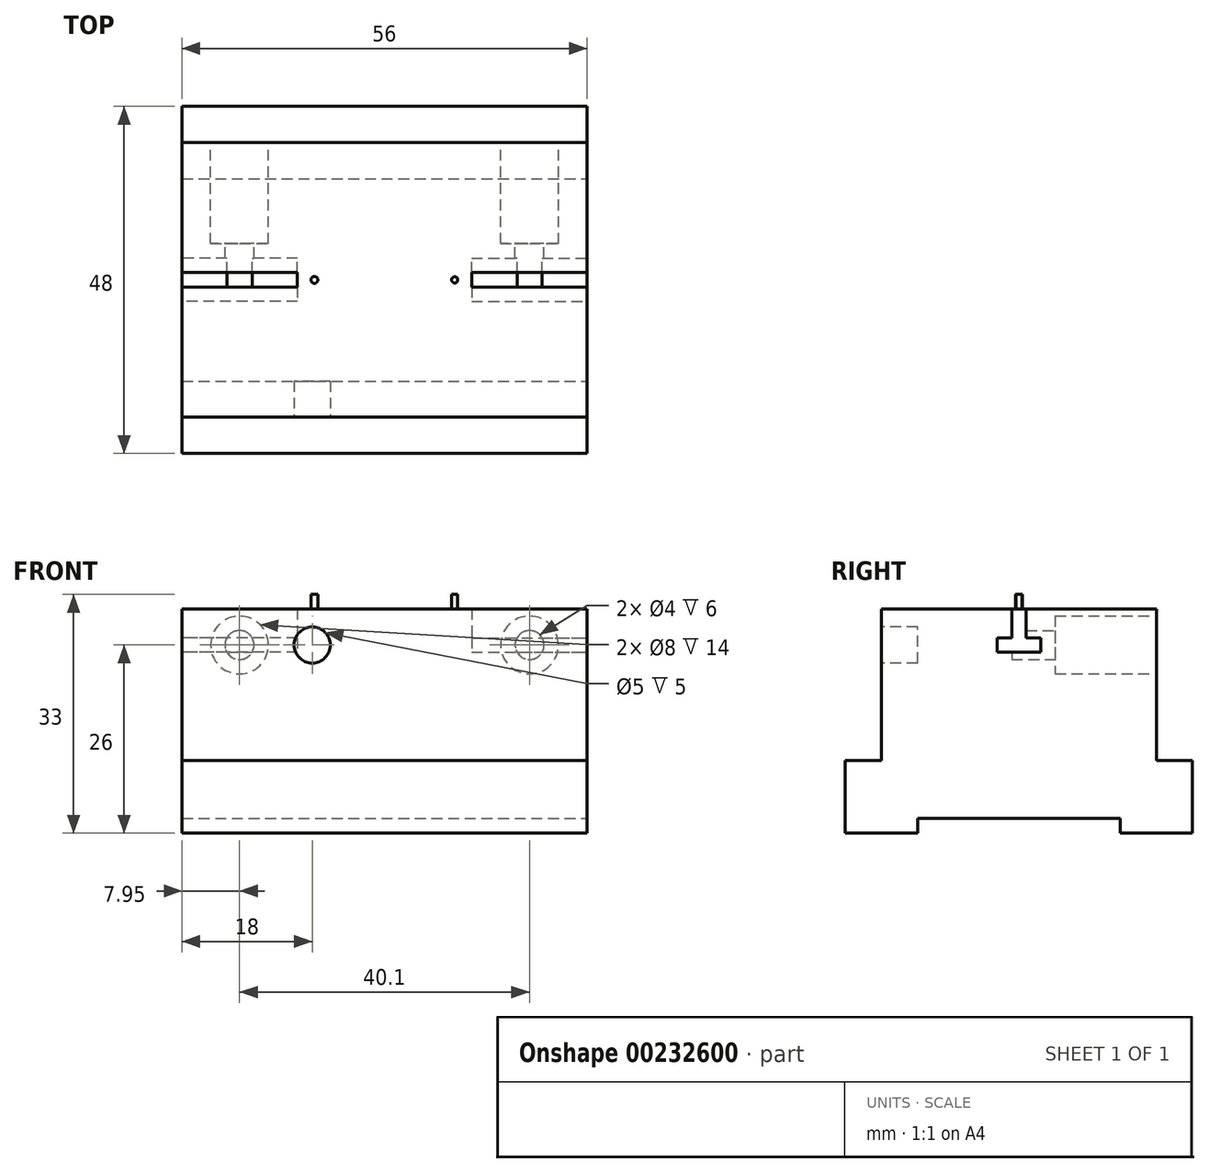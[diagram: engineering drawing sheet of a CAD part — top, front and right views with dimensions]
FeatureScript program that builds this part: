
annotation { "Feature Type Name" : "Feature", "Feature Type Description" : "" }
export const myFeature = defineFeature(function(context is Context, id is Id, definition is map)
    precondition{}
    {
        {
            var Q0;
            Q0=qCreatedBy(makeId("Top.planeOp"),FACE);
            var sketch = newSketch(context, id + "F0", { "sketchPlane" : qUnion([Q0])});
            skLineSegment(sketch, "E0.bottom", {"start": v(0, 0) * mm, "end": v(56, 0) * mm});
            skLineSegment(sketch, "E0.top", {"start": v(0, 48) * mm, "end": v(56, 48) * mm});
            skLineSegment(sketch, "E0.left", {"start": v(0, 0) * mm, "end": v(0, 48) * mm});
            skLineSegment(sketch, "E0.right", {"start": v(56, 0) * mm, "end": v(56, 48) * mm});
            skSolve(sketch);
        }
        {
            var Q0;
            Q0 = qSketchRegion(id + "F0", true);
            extrude(context, id + "F1", {"entities" : qUnion([Q0]), "oppositeDirection" : true, "depth" : 31 * mm});
        }
        {
            var Q0;
            Q0=qCreatedBy(makeId("Top.planeOp"),FACE);
            var sketch = newSketch(context, id + "F2", { "sketchPlane" : qUnion([Q0])});
            skCircle(sketch, "E1", {"center": v(18.3, 24) * mm, "radius": 0.47 * mm});
            skCircle(sketch, "E2", {"center": v(37.7, 24) * mm, "radius": 0.42 * mm});
            skSolve(sketch);
        }
        {
            var Q0;
            Q0 = qSketchRegion(id + "F2", true);
            extrude(context, id + "F3", {"entities" : qUnion([Q0]), "operationType" : NewBodyOperationType.ADD, "depth" : 2 * mm});
        }
        {
            var Q0;
            Q0=makeQuery(id+"F1.opExtrude","SWEPT_FACE",FACE,{"disambiguationData":[OSD([sQuery(id+"F0.wireOp",EDGE,"E0.right")])]});
            var sketch = newSketch(context, id + "F4", { "sketchPlane" : qUnion([Q0])});
            skLineSegment(sketch, "E3", {"start": v(23, 0) * mm, "end": v(23, -4) * mm});
            skLineSegment(sketch, "E4", {"start": v(23, -4) * mm, "end": v(21, -4) * mm});
            skLineSegment(sketch, "E5", {"start": v(21, -4) * mm, "end": v(21, -6) * mm});
            skLineSegment(sketch, "E6", {"start": v(21, -6) * mm, "end": v(27, -6) * mm});
            skLineSegment(sketch, "E7", {"start": v(27, -6) * mm, "end": v(27, -4) * mm});
            skLineSegment(sketch, "E8", {"start": v(27, -4) * mm, "end": v(25, -4) * mm});
            skLineSegment(sketch, "E9", {"start": v(25, -4) * mm, "end": v(25, 0) * mm});
            skLineSegment(sketch, "E10", {"start": v(25, 0) * mm, "end": v(23, 0) * mm});
            skSolve(sketch);
        }
        {
            var Q0;
            Q0=makeQuery(id+"F1.opExtrude","SWEPT_FACE",FACE,{"disambiguationData":[OSD([sQuery(id+"F0.wireOp",EDGE,"E0.left")])]});
            var sketch = newSketch(context, id + "F5", { "sketchPlane" : qUnion([Q0])});
            skLineSegment(sketch, "E11", {"start": v(-25, 0) * mm, "end": v(-25, -4) * mm});
            skLineSegment(sketch, "E12", {"start": v(-25, -4) * mm, "end": v(-27, -4) * mm});
            skLineSegment(sketch, "E13", {"start": v(-27, -4) * mm, "end": v(-27, -6) * mm});
            skLineSegment(sketch, "E14", {"start": v(-27, -6) * mm, "end": v(-21, -6) * mm});
            skLineSegment(sketch, "E15", {"start": v(-21, -6) * mm, "end": v(-21, -4) * mm});
            skLineSegment(sketch, "E16", {"start": v(-21, -4) * mm, "end": v(-23, -4) * mm});
            skLineSegment(sketch, "E17", {"start": v(-23, -4) * mm, "end": v(-23, 0) * mm});
            skLineSegment(sketch, "E18", {"start": v(-23, 0) * mm, "end": v(-25, 0) * mm});
            skSolve(sketch);
        }
        {
            var Q0;
            Q0 = qSketchRegion(id + "F4", true);
            extrude(context, id + "F6", {"entities" : qUnion([Q0]), "operationType" : NewBodyOperationType.REMOVE, "oppositeDirection" : true, "depth" : 15.95 * mm});
        }
        {
            var Q0;
            Q0 = qSketchRegion(id + "F5", true);
            extrude(context, id + "F7", {"entities" : qUnion([Q0]), "operationType" : NewBodyOperationType.REMOVE, "oppositeDirection" : true, "depth" : 15.95 * mm});
        }
        {
            var Q0;
            Q0=makeQuery(id+"F1.opExtrude","SWEPT_FACE",FACE,{"disambiguationData":[OSD([sQuery(id+"F0.wireOp",EDGE,"E0.bottom")])]});
            var sketch = newSketch(context, id + "F8", { "sketchPlane" : qUnion([Q0])});
            skCircle(sketch, "E19", {"center": v(18, -5) * mm, "radius": 2.5 * mm});
            skSolve(sketch);
        }
        {
            var Q0;
            Q0 = qSketchRegion(id + "F8", true);
            extrude(context, id + "F9", {"entities" : qUnion([Q0]), "operationType" : NewBodyOperationType.REMOVE, "oppositeDirection" : true, "depth" : 10 * mm});
        }
        {
            var Q0;
            Q0=makeQuery(id+"F1.opExtrude","SWEPT_FACE",FACE,{"disambiguationData":[OSD([sQuery(id+"F0.wireOp",EDGE,"E0.right")])]});
            var sketch = newSketch(context, id + "F10", { "sketchPlane" : qUnion([Q0])});
            skLineSegment(sketch, "E20", {"start": v(0, 0) * mm, "end": v(5, 0) * mm});
            skLineSegment(sketch, "E21", {"start": v(5, 0) * mm, "end": v(5, -21) * mm});
            skLineSegment(sketch, "E22", {"start": v(5, -21) * mm, "end": v(0, -21) * mm});
            skLineSegment(sketch, "E23", {"start": v(0, -21) * mm, "end": v(0, -31) * mm});
            skLineSegment(sketch, "E24", {"start": v(0, -31) * mm, "end": v(10, -31) * mm});
            skLineSegment(sketch, "E25", {"start": v(10, -31) * mm, "end": v(10, -29) * mm});
            skLineSegment(sketch, "E26", {"start": v(10, -29) * mm, "end": v(38, -29) * mm});
            skLineSegment(sketch, "E27", {"start": v(38, -29) * mm, "end": v(38, -31) * mm});
            skLineSegment(sketch, "E28", {"start": v(38, -31) * mm, "end": v(48, -31) * mm});
            skLineSegment(sketch, "E29", {"start": v(48, -31) * mm, "end": v(48, -21) * mm});
            skLineSegment(sketch, "E30", {"start": v(48, -21) * mm, "end": v(43, -21) * mm});
            skLineSegment(sketch, "E31", {"start": v(43, -21) * mm, "end": v(43, 0) * mm});
            skLineSegment(sketch, "E32", {"start": v(43, 0) * mm, "end": v(48, 0) * mm});
            skLineSegment(sketch, "E33", {"start": v(0, 0) * mm, "end": v(-4.97, 0) * mm});
            skLineSegment(sketch, "E34", {"start": v(-4.97, 0) * mm, "end": v(-4.97, -37.2) * mm});
            skLineSegment(sketch, "E35", {"start": v(-4.97, -37.2) * mm, "end": v(53.68, -37.2) * mm});
            skLineSegment(sketch, "E36", {"start": v(53.68, -37.2) * mm, "end": v(53.68, 0) * mm});
            skLineSegment(sketch, "E37", {"start": v(53.68, 0) * mm, "end": v(48, 0) * mm});
            skSolve(sketch);
        }
        {
            var Q0;
            Q0 = qSketchRegion(id + "F10", true);
            extrude(context, id + "F11", {"entities" : qUnion([Q0]), "operationType" : NewBodyOperationType.REMOVE, "endBound" : BoundingType.THROUGH_ALL, "oppositeDirection" : true, "depth" : 25 * mm});
        }
        {
            var Q0;
            Q0=makeQuery(id+"F11.boolean.opBoolean","COPY",FACE,{"derivedFrom":makeQuery(id+"F11.opExtrude","SWEPT_FACE",FACE,{"disambiguationData":[OSD([sQuery(id+"F10.wireOp",EDGE,"E31")])]})});
            var sketch = newSketch(context, id + "F12", { "sketchPlane" : qUnion([Q0])});
            skCircle(sketch, "E38", {"center": v(-48.05, -5) * mm, "radius": 2 * mm});
            skCircle(sketch, "E39", {"center": v(-7.95, -5) * mm, "radius": 2 * mm});
            skSolve(sketch);
        }
        {
            var Q0;
            Q0 = qSketchRegion(id + "F12", true);
            extrude(context, id + "F13", {"entities" : qUnion([Q0]), "operationType" : NewBodyOperationType.REMOVE, "oppositeDirection" : true, "depth" : 20 * mm});
        }
        {
            var Q0;
            Q0=makeQuery(id+"F11.boolean.opBoolean","COPY",FACE,{"derivedFrom":makeQuery(id+"F11.opExtrude","SWEPT_FACE",FACE,{"disambiguationData":[OSD([sQuery(id+"F10.wireOp",EDGE,"E31")])]})});
            var sketch = newSketch(context, id + "F14", { "sketchPlane" : qUnion([Q0])});
            skCircle(sketch, "E40", {"center": v(-48.05, -5) * mm, "radius": 4 * mm});
            skCircle(sketch, "E41", {"center": v(-7.95, -5) * mm, "radius": 4 * mm});
            skSolve(sketch);
        }
        {
            var Q0;
            Q0 = qSketchRegion(id + "F14", true);
            extrude(context, id + "F15", {"entities" : qUnion([Q0]), "operationType" : NewBodyOperationType.REMOVE, "oppositeDirection" : true, "depth" : 14 * mm});
        }
    });
